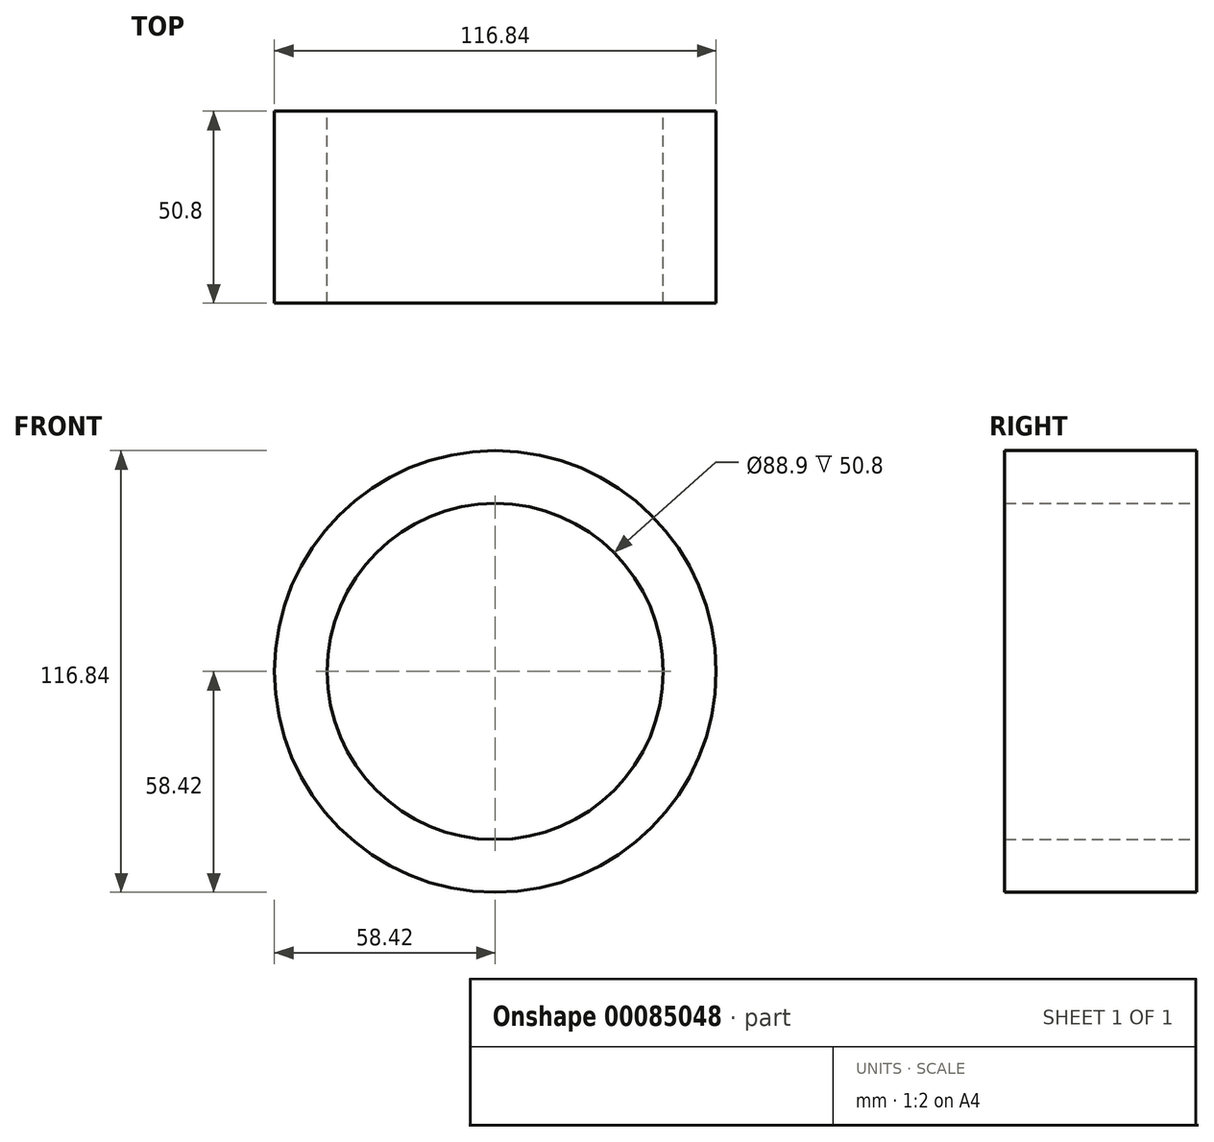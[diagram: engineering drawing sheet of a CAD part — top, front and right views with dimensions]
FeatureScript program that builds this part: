
annotation { "Feature Type Name" : "Feature", "Feature Type Description" : "" }
export const myFeature = defineFeature(function(context is Context, id is Id, definition is map)
    precondition{}
    {
        {
            var Q0;
            Q0=qCreatedBy(makeId("Front.planeOp"),FACE);
            var sketch = newSketch(context, id + "F0", { "sketchPlane" : qUnion([Q0])});
            skCircle(sketch, "E0", {"center": v(0, 0) * mm, "radius": 44.45 * mm});
            skCircle(sketch, "E1", {"center": v(0, 0) * mm, "radius": 58.42 * mm});
            skSolve(sketch);
        }
        {
            var Q0;
            Q0 = qSketchRegion(id + "F0", true);
            extrude(context, id + "F1", {"entities" : qUnion([Q0]), "depth" : 50.8 * mm});
        }
    });
